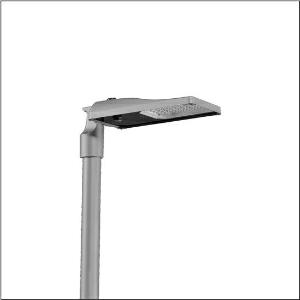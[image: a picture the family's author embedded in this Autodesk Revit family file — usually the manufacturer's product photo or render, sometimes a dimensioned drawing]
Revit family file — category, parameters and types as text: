
# Revit family: streetlight_sl_31_mini___st1_0a_5xh6d31t08ha_30ca
name_source: partatom
category: Lighting Fixtures
units: mm (PartAtom-declared; Revit-internal decimal feet)

## family parameters
Cut with Voids When Loaded = No
Host = Face
Light Source = No
Part Type = Normal
Room Calculation Point = No
Round Connector Dimension = Use Diameter
Shared = No

## types (1)
- --- (1 x LED, 9230 lm, 68.3 W, 3000K)
    Apparent Load = 68 VA
    CIE Flux Codes = 37 72 97 100 100
    Color Rendering = 70
    Color Temperature = 3000K
    Default Elevation = 1800 mm
    Description = Streetlight SL 31 mini D4i, Desk-Remote mast luminaire for post-top, side-entry; light control with lens of PMMA; light distribution: ST1.0a, direct asymmetric distribution, for standard-compliant lighting for roads and squares; LED: luminous flux: 9.230lm, light colour: 730, colour temperature: 3000K; luminous efficacy: 135,1lm/W; control: pre-setting: logarithmic dimming characteristic, flexible luminous flux parameterisation, time-dependent luminous flux control, constant luminous flux control, power reduction, intelligent temperature release in ECG and LED module, overheat protection; luminaire housing, of diecast aluminium, SITECO metallic grey (DB 702S), corrosivity category C5 high according to DIN EN ISO 12944; cover of toughened safety glass, transparent, opened without tools; mast flange of diecast aluminium, SITECO metallic grey (DB 702S), spigot size: 76/60mm, mast flange included unmounted; with cable H07RN-F 2x 1.5mm², cable length: 8,5m, connection cable pre-assembled; mains connection: 220..240V, AC, 50/60Hz; power consumption (at start of service life): 68,3W / (at end of service life): 74,5W / (with reduced operation 50%): 29,5W; protection rating (complete): IP66; insulation class (complete): insulation class II (safety insulation); impact resistance: IK09; certification: CE, ENEC, ENEC+, VDE, UKCA, ZD4i; permissible operating ambient temperature for outdoor applications: -40..+50°C; packaging unit: 1 piece

Light Distribution: ST1.0a
    Height = 76 mm
    Lamp = 1 x LED
    Lamp Light Flux = 9230 lm
    Lamp Power = 68.3 W
    Lamp count = 1
    Length = 547 mm
    Luminous efficacy = 135 lm/W
    Manufacturer = Siteco
    ModVariant = No
    Model = 5XH6D31T08HA
    Mounting Place = Pole
    Mounting Type = Pole top
    Number of Poles = 1
    OnlyDefault = Yes
    Power Factor = 1
    Product Name = Streetlight SL 31 mini | ST1.0a
    Product group = mast luminaire | pylon top
    ProductGroupID = 6100
    Protection Class = Protection class II
    Protection Degree = IP 66
    RLX_Detail_Level = 1
    RLX_Emergency_Light_Flux = 0 lm
    RLX_Emergency_Type = 0
    RLX_Emergency_Type_DB = No
    RlxData = <blob elided: 24361 chars, md5=5bea9824>
    Socket = socket
    Standby Power = 0 W
    System Light Flux = 9230 lm
    System Power = 68 W
    Type Comments = factory setting: luminous flux: 100 % | dim-lin: 254 | 692 mA
    Type Image = l_1300332.jpg
    URL = http://relux.com
    VarID = @adj_021845
    Voltage = 0 V
    Weight = 0.00 kg
    Width = 265 mm

## geometry (parser evidence)
native form markers: Blend x4, Sweep x11
no freeform markers — native parametric forms only
